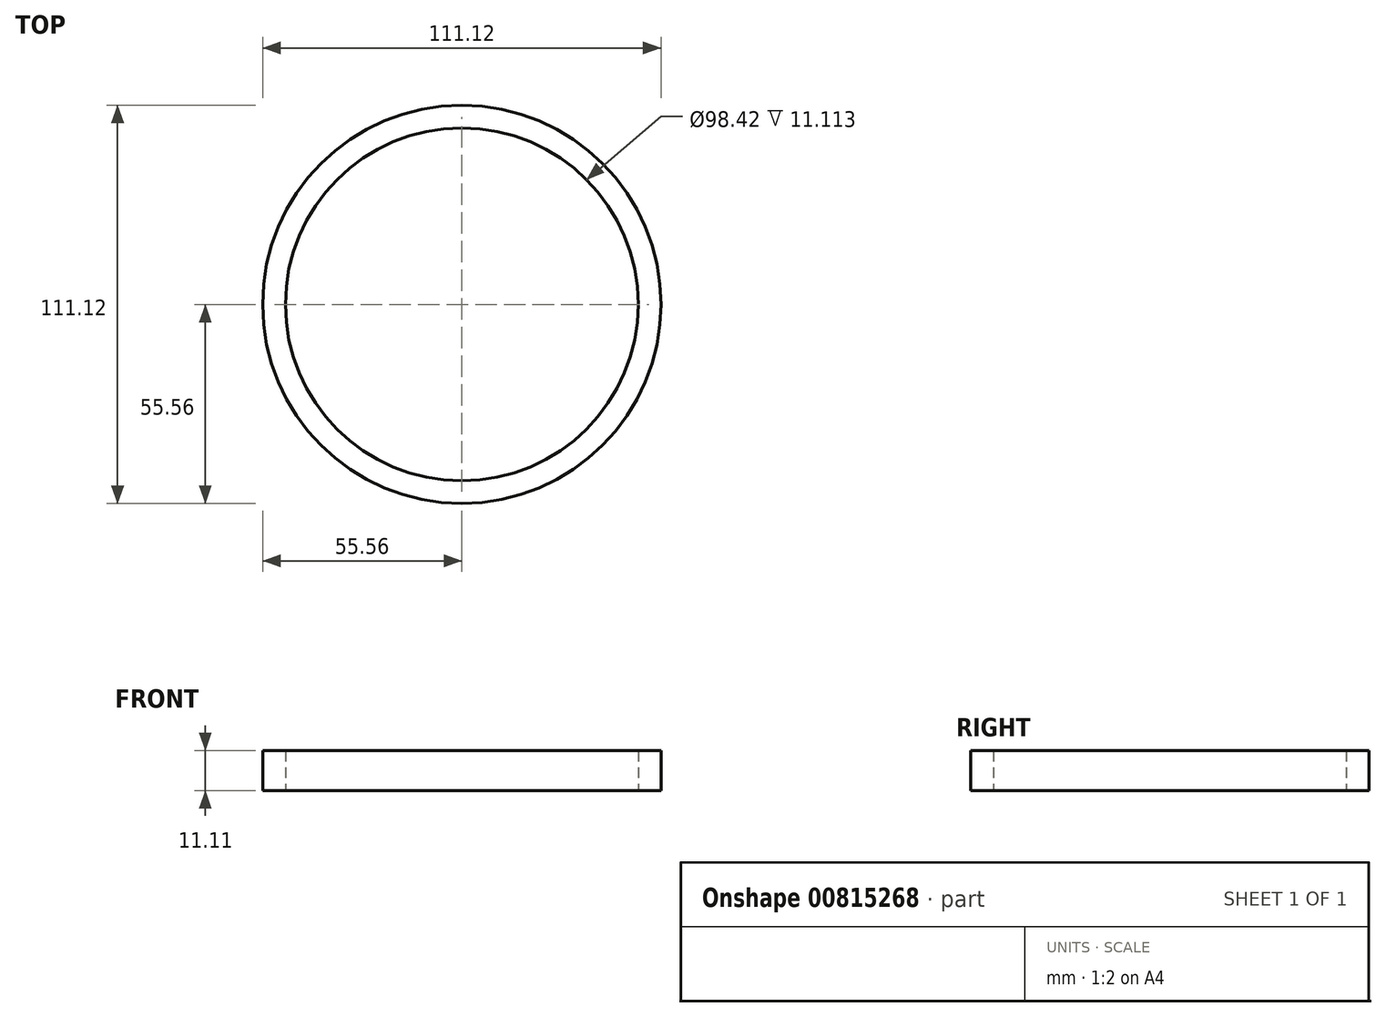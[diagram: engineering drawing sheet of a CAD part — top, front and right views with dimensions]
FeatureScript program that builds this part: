
annotation { "Feature Type Name" : "Feature", "Feature Type Description" : "" }
export const myFeature = defineFeature(function(context is Context, id is Id, definition is map)
    precondition{}
    {
        {
            var Q0;
            Q0=qCreatedBy(makeId("Top.planeOp"),FACE);
            var sketch = newSketch(context, id + "F0", { "sketchPlane" : qUnion([Q0])});
            skCircle(sketch, "E0", {"center": v(0, 0) * mm, "radius": 49.21 * mm});
            skCircle(sketch, "E1", {"center": v(0, 0) * mm, "radius": 55.56 * mm});
            skSolve(sketch);
        }
        {
            var Q0;
            Q0=makeQuery(id+"F0.imprint","IMPRINT",FACE,{"disambiguationData":[TD([[makeQuery(id+"F0.imprint","IMPRINT",EDGE,{"derivedFrom":sQuery(id+"F0.wireOp",EDGE,"E0")}),-1.0]])]});
            extrude(context, id + "F1", {"entities" : qUnion([Q0]), "depth" : 11.1 * mm, "offsetDistance" : 25.4 * mm});
        }
    });
